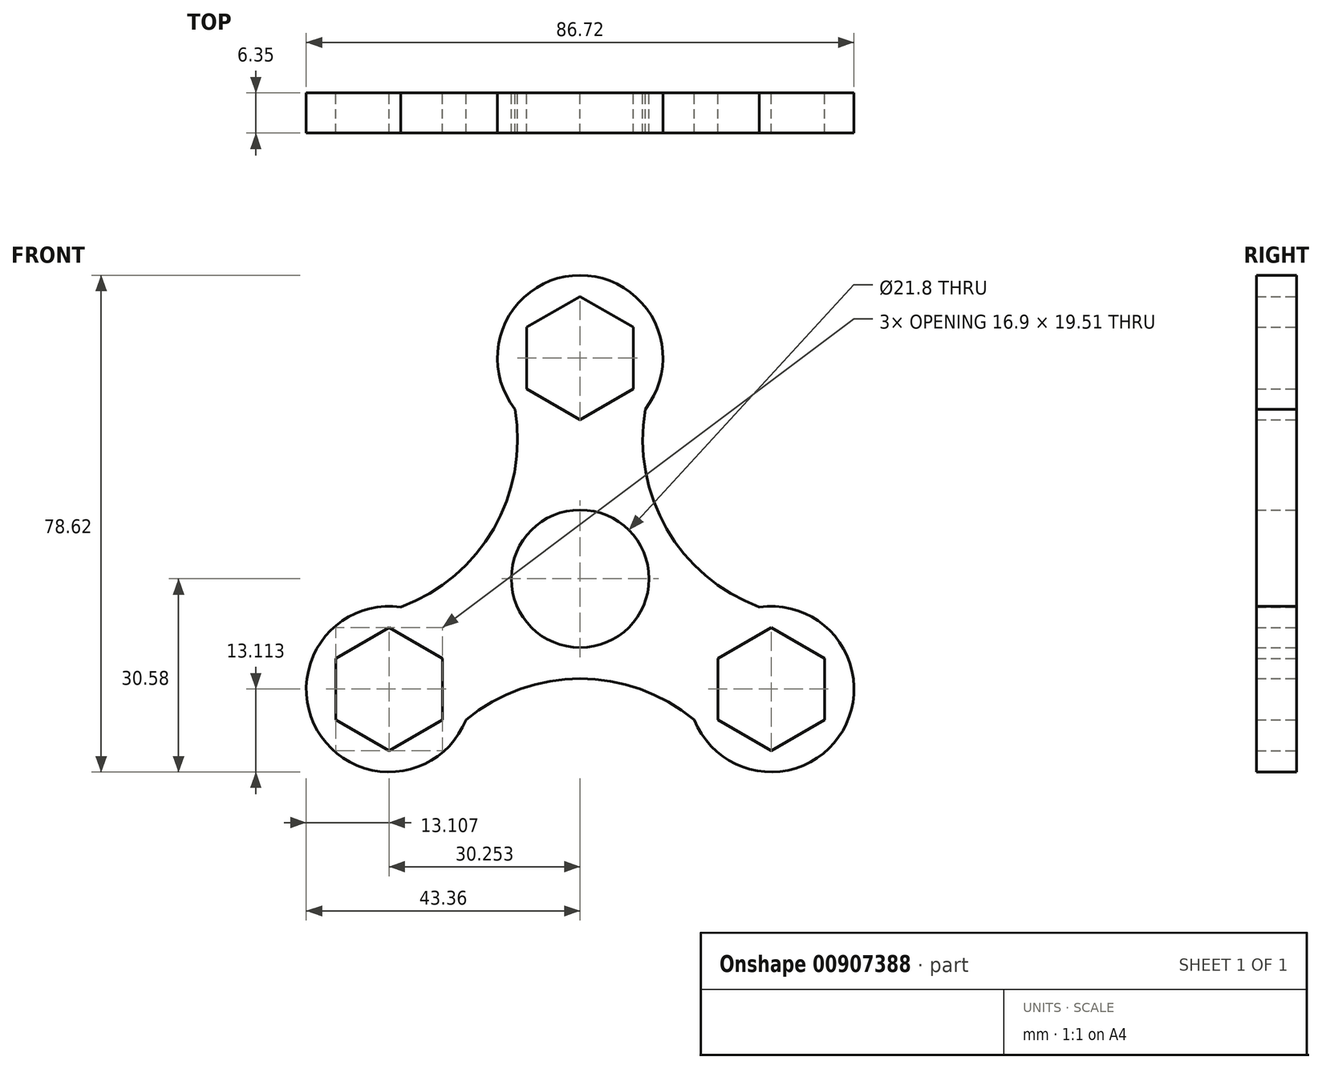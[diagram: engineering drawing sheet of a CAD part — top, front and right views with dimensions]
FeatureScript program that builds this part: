
annotation { "Feature Type Name" : "Feature", "Feature Type Description" : "" }
export const myFeature = defineFeature(function(context is Context, id is Id, definition is map)
    precondition{}
    {
        {
            var Q0;
            Q0=qCreatedBy(makeId("Front.planeOp"),FACE);
            var sketch = newSketch(context, id + "F0", { "sketchPlane" : qUnion([Q0])});
            skCircle(sketch, "E0", {"center": v(0, 0) * mm, "radius": 10.9 * mm});
            skArc(sketch, "E1", {"start": v(10.3, 26.83) * mm, "mid": v(0, 48.04) * mm, "end": v(-10.3, 26.83) * mm});
            skLineSegment(sketch, "E2.0", {"start": v(8.45, 39.81) * mm, "end": v(8.45, 30.05) * mm});
            skLineSegment(sketch, "E2.1", {"start": v(8.45, 30.05) * mm, "end": v(0, 25.18) * mm});
            skLineSegment(sketch, "E2.2", {"start": v(0, 25.18) * mm, "end": v(-8.45, 30.05) * mm});
            skLineSegment(sketch, "E2.3", {"start": v(-8.45, 30.05) * mm, "end": v(-8.45, 39.81) * mm});
            skLineSegment(sketch, "E2.4", {"start": v(-8.45, 39.81) * mm, "end": v(0, 44.7) * mm});
            skLineSegment(sketch, "E2.5", {"start": v(0, 44.7) * mm, "end": v(8.45, 39.81) * mm});
            skPoint(sketch, "E2.0.midPoint", {"position": v(8.45, 34.93) * mm});
            skArc(sketch, "E3.1.0", {"start": v(-28.4, -4.49) * mm, "mid": v(-41.6, -24.02) * mm, "end": v(-18.08, -22.35) * mm});
            skPoint(sketch, "E3.1.2", {"position": v(-34.48, -10.15) * mm});
            skLineSegment(sketch, "E3.1.3", {"start": v(-21.8, -22.35) * mm, "end": v(-30.25, -27.22) * mm});
            skLineSegment(sketch, "E3.1.4", {"start": v(-38.7, -12.59) * mm, "end": v(-30.25, -7.7) * mm});
            skLineSegment(sketch, "E3.1.5", {"start": v(-38.7, -22.35) * mm, "end": v(-38.7, -12.59) * mm});
            skLineSegment(sketch, "E3.1.6", {"start": v(-30.25, -27.22) * mm, "end": v(-38.7, -22.35) * mm});
            skLineSegment(sketch, "E3.1.7", {"start": v(-21.8, -12.59) * mm, "end": v(-21.8, -22.35) * mm});
            skLineSegment(sketch, "E3.1.8", {"start": v(-30.25, -7.7) * mm, "end": v(-21.8, -12.59) * mm});
            skArc(sketch, "E3.2.0", {"start": v(18.08, -22.35) * mm, "mid": v(41.6, -24.02) * mm, "end": v(28.4, -4.49) * mm});
            skPoint(sketch, "E3.2.2", {"position": v(26.03, -24.78) * mm});
            skLineSegment(sketch, "E3.2.3", {"start": v(30.25, -7.7) * mm, "end": v(38.7, -12.59) * mm});
            skLineSegment(sketch, "E3.2.4", {"start": v(30.25, -27.22) * mm, "end": v(21.8, -22.35) * mm});
            skLineSegment(sketch, "E3.2.5", {"start": v(38.7, -22.35) * mm, "end": v(30.25, -27.22) * mm});
            skLineSegment(sketch, "E3.2.6", {"start": v(38.7, -12.59) * mm, "end": v(38.7, -22.35) * mm});
            skLineSegment(sketch, "E3.2.7", {"start": v(21.8, -12.59) * mm, "end": v(30.25, -7.7) * mm});
            skLineSegment(sketch, "E3.2.8", {"start": v(21.8, -22.35) * mm, "end": v(21.8, -12.59) * mm});
            skArc(sketch, "E4", {"start": v(18.08, -22.35) * mm, "mid": v(0, -15.82) * mm, "end": v(-18.08, -22.35) * mm});
            skArc(sketch, "E5.1.0", {"start": v(10.3, 26.83) * mm, "mid": v(13.7, 7.91) * mm, "end": v(28.4, -4.49) * mm});
            skArc(sketch, "E5.2.0", {"start": v(-28.4, -4.49) * mm, "mid": v(-13.7, 7.91) * mm, "end": v(-10.3, 26.83) * mm});
            skSolve(sketch);
        }
        {
            var Q0;
            Q0=makeQuery(id+"F0.imprint","IMPRINT",FACE,{"disambiguationData":[TD([[makeQuery(id+"F0.imprint","IMPRINT",EDGE,{"derivedFrom":sQuery(id+"F0.wireOp",EDGE,"E0")}),-1.0]])]});
            var Q1;
            Q1=makeQuery(id+"F0.imprint","IMPRINT",FACE,{"disambiguationData":[TD([[makeQuery(id+"F0.imprint","IMPRINT",EDGE,{"derivedFrom":sQuery(id+"F0.wireOp",EDGE,"E3.1.3")}),1.0]])]});
            var Q2;
            Q2=makeQuery(id+"F0.imprint","IMPRINT",FACE,{"disambiguationData":[TD([[makeQuery(id+"F0.imprint","IMPRINT",EDGE,{"derivedFrom":sQuery(id+"F0.wireOp",EDGE,"E3.2.3")}),1.0]])]});
            var Q3;
            Q3=makeQuery(id+"F0.imprint","IMPRINT",FACE,{"disambiguationData":[TD([[makeQuery(id+"F0.imprint","IMPRINT",EDGE,{"derivedFrom":sQuery(id+"F0.wireOp",EDGE,"E2.0")}),1.0]])]});
            extrude(context, id + "F1", {"entities" : qUnion([Q0, Q1, Q2, Q3]), "depth" : 6.35 * mm, "offsetDistance" : 25.4 * mm});
        }
    });
